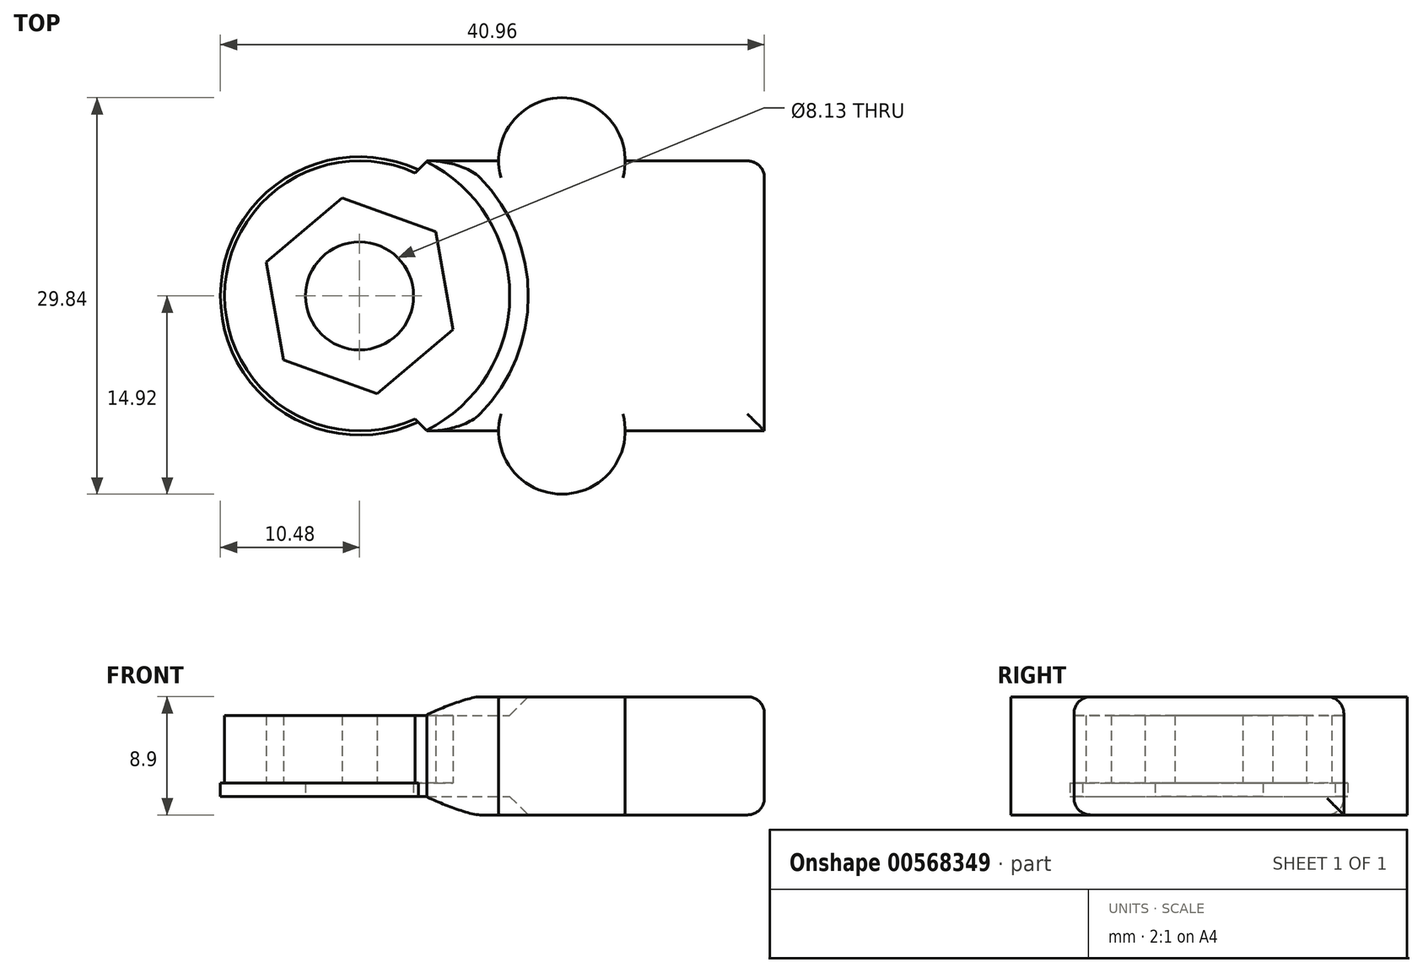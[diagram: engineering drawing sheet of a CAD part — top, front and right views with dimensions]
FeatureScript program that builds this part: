
annotation { "Feature Type Name" : "Feature", "Feature Type Description" : "" }
export const myFeature = defineFeature(function(context is Context, id is Id, definition is map)
    precondition{}
    {
        {
            var Q0;
            Q0=qCreatedBy(makeId("Top.planeOp"),FACE);
            var sketch = newSketch(context, id + "F0", { "sketchPlane" : qUnion([Q0])});
            skCircle(sketch, "E0.cCircle", {"center": v(0, 0) * mm, "radius": 6.48 * mm, "construction": true});
            skLineSegment(sketch, "E0.0", {"start": v(-7.03, 2.55) * mm, "end": v(-1.31, 7.36) * mm});
            skLineSegment(sketch, "E0.1", {"start": v(-1.31, 7.36) * mm, "end": v(5.72, 4.82) * mm});
            skLineSegment(sketch, "E0.2", {"start": v(5.72, 4.82) * mm, "end": v(7.03, -2.55) * mm});
            skLineSegment(sketch, "E0.3", {"start": v(7.03, -2.55) * mm, "end": v(1.31, -7.36) * mm});
            skLineSegment(sketch, "E0.4", {"start": v(1.31, -7.36) * mm, "end": v(-5.72, -4.82) * mm});
            skLineSegment(sketch, "E0.5", {"start": v(-5.72, -4.82) * mm, "end": v(-7.03, 2.55) * mm});
            skPoint(sketch, "E0.0.midPoint", {"position": v(-4.17, 4.95) * mm});
            skLineSegment(sketch, "E1.trimOffspring", {"start": v(4.6, -4.6) * mm, "end": v(4.58, -4.58) * mm});
            skCircle(sketch, "E2", {"center": v(0, 0) * mm, "radius": 10.16 * mm});
            skLineSegment(sketch, "E3.left", {"start": v(0, 10.2) * mm, "end": v(0, -10.12) * mm});
            skLineSegment(sketch, "E4.bottom", {"start": v(5.08, 10.16) * mm, "end": v(10.48, 10.16) * mm});
            skLineSegment(sketch, "E4.top", {"start": v(5.08, -10.16) * mm, "end": v(10.48, -10.16) * mm});
            skLineSegment(sketch, "E4.right", {"start": v(30.48, 10.16) * mm, "end": v(30.48, -10.16) * mm});
            skArc(sketch, "E5", {"start": v(20, 10.16) * mm, "mid": v(15.24, 14.92) * mm, "end": v(10.48, 10.16) * mm});
            skArc(sketch, "E6", {"start": v(10.48, -10.16) * mm, "mid": v(15.24, -14.92) * mm, "end": v(20, -10.16) * mm});
            skLineSegment(sketch, "E7", {"start": v(5.08, 10.16) * mm, "end": v(4.18, 9.26) * mm});
            skLineSegment(sketch, "E8", {"start": v(5.08, -10.16) * mm, "end": v(4.18, -9.26) * mm});
            skLineSegment(sketch, "E9.trimOffspring", {"start": v(20, 10.16) * mm, "end": v(30.48, 10.16) * mm});
            skLineSegment(sketch, "E10.trimOffspring", {"start": v(20, -10.16) * mm, "end": v(30.48, -10.16) * mm});
            skArc(sketch, "E11.MirrorCS", {"start": v(-20, 10.16) * mm, "mid": v(-15.24, 14.92) * mm, "end": v(-10.48, 10.16) * mm});
            skLineSegment(sketch, "E12.MirrorCS", {"start": v(-5.08, 10.16) * mm, "end": v(-10.48, 10.16) * mm});
            skLineSegment(sketch, "E13.MirrorCS", {"start": v(-5.08, 10.16) * mm, "end": v(-4.18, 9.26) * mm});
            skLineSegment(sketch, "E14.MirrorCS", {"start": v(-20, 10.16) * mm, "end": v(-30.48, 10.16) * mm});
            skLineSegment(sketch, "E15.MirrorCS", {"start": v(-30.48, 10.16) * mm, "end": v(-30.48, -10.16) * mm});
            skLineSegment(sketch, "E16.MirrorCS", {"start": v(-5.08, -10.16) * mm, "end": v(-4.18, -9.26) * mm});
            skArc(sketch, "E17.MirrorCS", {"start": v(-10.48, -10.16) * mm, "mid": v(-15.24, -14.92) * mm, "end": v(-20, -10.16) * mm});
            skLineSegment(sketch, "E18.MirrorCS", {"start": v(-5.08, -10.16) * mm, "end": v(-10.48, -10.16) * mm});
            skLineSegment(sketch, "E19.MirrorCS", {"start": v(-20, -10.16) * mm, "end": v(-30.48, -10.16) * mm});
            skSolve(sketch);
        }
        {
            var Q0;
            {var subQ4=sQuery(id+"F0.wireOp",EDGE,"E0.0");Q0=makeQuery(id+"F0.imprint","IMPRINT",FACE,{"disambiguationData":[TD([[makeQuery(id+"F0.imprint","IMPRINT",EDGE,{"derivedFrom":subQ4}),1.0]])]});}
            extrude(context, id + "F1", {"entities" : qUnion([Q0]), "endBound" : BoundingType.SYMMETRIC, "depth" : 6.1 * mm, "offsetDistance" : 25.4 * mm});
        }
        {
            var Q0;
            Q0=makeQuery(id+"F0.imprint","IMPRINT",FACE,{"disambiguationData":[TD([[makeQuery(id+"F0.imprint","IMPRINT",EDGE,{"derivedFrom":sQuery(id+"F0.wireOp",EDGE,"E11.MirrorCS")}),-1.0]])]});
            var Q1;
            Q1=makeQuery(id+"F0.imprint","IMPRINT",FACE,{"disambiguationData":[TD([[makeQuery(id+"F0.imprint","IMPRINT",EDGE,{"derivedFrom":sQuery(id+"F0.wireOp",EDGE,"E4.bottom")}),-1.0]])]});
            extrude(context, id + "F2", {"entities" : qUnion([Q0, Q1]), "operationType" : NewBodyOperationType.ADD, "endBound" : BoundingType.SYMMETRIC, "depth" : 8.9 * mm, "offsetDistance" : 25.4 * mm});
        }
        {
            var Q0;
            {var subQ0=sQuery(id+"F0.wireOp",EDGE,"E2");Q0=makeQuery(id+"F2.opExtrude","CAP_EDGE",EDGE,{"disambiguationData":[OSD([subQ0]),TDD([makeQuery(id+"F0.imprint","IMPRINT",EDGE,{"disambiguationData":[TD([[makeQuery(id+"F0.imprint","INTERSECT",VERTEX,{"derivedFrom":[subQ0,sQuery(id+"F0.wireOp",EDGE,"E13.MirrorCS")]}),-1.0]])],"derivedFrom":subQ0})])],"isStart":false});}
            var Q1;
            {var subQ0=sQuery(id+"F0.wireOp",EDGE,"E2");Q1=makeQuery(id+"F2.opExtrude","CAP_EDGE",EDGE,{"disambiguationData":[OSD([subQ0]),TDD([makeQuery(id+"F0.imprint","IMPRINT",EDGE,{"disambiguationData":[TD([[makeQuery(id+"F0.imprint","INTERSECT",VERTEX,{"derivedFrom":[subQ0,sQuery(id+"F0.wireOp",EDGE,"E7")]}),1.0]])],"derivedFrom":subQ0})])],"isStart":false});}
            var Q2;
            {var subQ0=sQuery(id+"F0.wireOp",EDGE,"E2");Q2=makeQuery(id+"F2.opExtrude","CAP_EDGE",EDGE,{"disambiguationData":[OSD([subQ0]),TDD([makeQuery(id+"F0.imprint","IMPRINT",EDGE,{"disambiguationData":[TD([[makeQuery(id+"F0.imprint","INTERSECT",VERTEX,{"derivedFrom":[subQ0,sQuery(id+"F0.wireOp",EDGE,"E7")]}),1.0]])],"derivedFrom":subQ0})])],"isStart":true});}
            var Q3;
            {var subQ0=sQuery(id+"F0.wireOp",EDGE,"E2");Q3=makeQuery(id+"F2.opExtrude","CAP_EDGE",EDGE,{"disambiguationData":[OSD([subQ0]),TDD([makeQuery(id+"F0.imprint","IMPRINT",EDGE,{"disambiguationData":[TD([[makeQuery(id+"F0.imprint","INTERSECT",VERTEX,{"derivedFrom":[subQ0,sQuery(id+"F0.wireOp",EDGE,"E13.MirrorCS")]}),-1.0]])],"derivedFrom":subQ0})])],"isStart":true});}
            chamfer(context, id + "F3", {"entities" : qUnion([Q0, Q1, Q2, Q3]), "width" : 2.54 * mm, "tangentPropagation" : true});
        }
        {
            var Q0;
            Q0=makeQuery(id+"F2.opExtrude","CAP_EDGE",EDGE,{"disambiguationData":[OSD([sQuery(id+"F0.wireOp",EDGE,"E19.MirrorCS")])],"isStart":false});
            var Q1;
            Q1=makeQuery(id+"F2.opExtrude","CAP_EDGE",EDGE,{"disambiguationData":[OSD([sQuery(id+"F0.wireOp",EDGE,"E15.MirrorCS")])],"isStart":false});
            var Q2;
            Q2=makeQuery(id+"F2.opExtrude","CAP_EDGE",EDGE,{"disambiguationData":[OSD([sQuery(id+"F0.wireOp",EDGE,"E14.MirrorCS")])],"isStart":false});
            var Q3;
            Q3=makeQuery(id+"F2.opExtrude","CAP_EDGE",EDGE,{"disambiguationData":[OSD([sQuery(id+"F0.wireOp",EDGE,"E10.trimOffspring")])],"isStart":false});
            var Q4;
            Q4=makeQuery(id+"F2.opExtrude","CAP_EDGE",EDGE,{"disambiguationData":[OSD([sQuery(id+"F0.wireOp",EDGE,"E4.right")])],"isStart":false});
            var Q5;
            Q5=makeQuery(id+"F2.opExtrude","CAP_EDGE",EDGE,{"disambiguationData":[OSD([sQuery(id+"F0.wireOp",EDGE,"E9.trimOffspring")])],"isStart":false});
            var Q6;
            Q6=makeQuery(id+"F2.opExtrude","CAP_EDGE",EDGE,{"disambiguationData":[OSD([sQuery(id+"F0.wireOp",EDGE,"E19.MirrorCS")])],"isStart":true});
            var Q7;
            Q7=makeQuery(id+"F2.opExtrude","SWEPT_EDGE",EDGE,{"disambiguationData":[OSD([sQuery(id+"F0.wireOp",EDGE,"E15.MirrorCS"),sQuery(id+"F0.wireOp",EDGE,"E19.MirrorCS")])]});
            var Q8;
            Q8=makeQuery(id+"F2.opExtrude","CAP_EDGE",EDGE,{"disambiguationData":[OSD([sQuery(id+"F0.wireOp",EDGE,"E10.trimOffspring")])],"isStart":true});
            var Q9;
            Q9=makeQuery(id+"F2.opExtrude","CAP_EDGE",EDGE,{"disambiguationData":[OSD([sQuery(id+"F0.wireOp",EDGE,"E4.right")])],"isStart":true});
            var Q10;
            Q10=makeQuery(id+"F2.opExtrude","SWEPT_EDGE",EDGE,{"disambiguationData":[OSD([sQuery(id+"F0.wireOp",EDGE,"E4.right"),sQuery(id+"F0.wireOp",EDGE,"E9.trimOffspring")])]});
            var Q11;
            Q11=makeQuery(id+"F2.opExtrude","SWEPT_EDGE",EDGE,{"disambiguationData":[OSD([sQuery(id+"F0.wireOp",EDGE,"E14.MirrorCS"),sQuery(id+"F0.wireOp",EDGE,"E15.MirrorCS")])]});
            var Q12;
            Q12=makeQuery(id+"F2.opExtrude","CAP_EDGE",EDGE,{"disambiguationData":[OSD([sQuery(id+"F0.wireOp",EDGE,"E14.MirrorCS")])],"isStart":true});
            var Q13;
            Q13=makeQuery(id+"F2.opExtrude","CAP_EDGE",EDGE,{"disambiguationData":[OSD([sQuery(id+"F0.wireOp",EDGE,"E15.MirrorCS")])],"isStart":true});
            var Q14;
            Q14=makeQuery(id+"F2.opExtrude","CAP_EDGE",EDGE,{"disambiguationData":[OSD([sQuery(id+"F0.wireOp",EDGE,"E12.MirrorCS")])],"isStart":false});
            var Q15;
            Q15=makeQuery(id+"F2.opExtrude","CAP_EDGE",EDGE,{"disambiguationData":[OSD([sQuery(id+"F0.wireOp",EDGE,"E4.bottom")])],"isStart":false});
            var Q16;
            Q16=makeQuery(id+"F2.opExtrude","CAP_EDGE",EDGE,{"disambiguationData":[OSD([sQuery(id+"F0.wireOp",EDGE,"E18.MirrorCS")])],"isStart":false});
            var Q17;
            Q17=makeQuery(id+"F2.opExtrude","CAP_EDGE",EDGE,{"disambiguationData":[OSD([sQuery(id+"F0.wireOp",EDGE,"E4.top")])],"isStart":false});
            var Q18;
            Q18=makeQuery(id+"F2.opExtrude","CAP_EDGE",EDGE,{"disambiguationData":[OSD([sQuery(id+"F0.wireOp",EDGE,"E4.bottom")])],"isStart":true});
            var Q19;
            Q19=makeQuery(id+"F2.opExtrude","CAP_EDGE",EDGE,{"disambiguationData":[OSD([sQuery(id+"F0.wireOp",EDGE,"E12.MirrorCS")])],"isStart":true});
            var Q20;
            Q20=makeQuery(id+"F2.opExtrude","CAP_EDGE",EDGE,{"disambiguationData":[OSD([sQuery(id+"F0.wireOp",EDGE,"E18.MirrorCS")])],"isStart":true});
            var Q21;
            Q21=makeQuery(id+"F2.opExtrude","CAP_EDGE",EDGE,{"disambiguationData":[OSD([sQuery(id+"F0.wireOp",EDGE,"E4.top")])],"isStart":true});
            fillet(context, id + "F4", {"entities" : qUnion([Q0, Q1, Q2, Q3, Q4, Q5, Q6, Q7, Q8, Q9, Q10, Q11, Q12, Q13, Q14, Q15, Q16, Q17, Q18, Q19, Q20, Q21]), "radius" : 1.27 * mm, "tangentPropagation" : true, "allowEdgeOverflow" : false});
        }
        {
            var Q0;
            Q0=makeQuery(id+"F1.opExtrude","CAP_FACE",FACE,{"disambiguationData":[OSD([sQuery(id+"F0.wireOp",EDGE,"E0.0"),sQuery(id+"F0.wireOp",EDGE,"E0.1"),sQuery(id+"F0.wireOp",EDGE,"E0.2"),sQuery(id+"F0.wireOp",EDGE,"E0.3"),sQuery(id+"F0.wireOp",EDGE,"E0.4"),sQuery(id+"F0.wireOp",EDGE,"E0.5"),sQuery(id+"F0.wireOp",EDGE,"RWQ8MwqZ-qSjk-59TD-cotx-tmdDIhJuCybJ")])],"isStart":true});
            var sketch = newSketch(context, id + "F5", { "sketchPlane" : qUnion([Q0])});
            skCircle(sketch, "E20", {"center": v(0, 0) * mm, "radius": 10.48 * mm});
            skCircle(sketch, "E21", {"center": v(0, 0) * mm, "radius": 4.06 * mm});
            skSolve(sketch);
        }
        {
            var Q0;
            Q0=makeQuery(id+"F5.imprint","IMPRINT",FACE,{"disambiguationData":[TD([[makeQuery(id+"F5.imprint","IMPRINT",EDGE,{"derivedFrom":sQuery(id+"F5.wireOp",EDGE,"E20")}),1.0]])]});
            var Q1;
            Q1=makeQuery(id+"F5.imprint","IMPRINT",FACE,{"disambiguationData":[TD([[makeQuery(id+"F5.imprint","IMPRINT",EDGE,{"derivedFrom":sQuery(id+"F5.wireOp",EDGE,"E21")}),-1.0]])]});
            extrude(context, id + "F6", {"entities" : qUnion([Q0, Q1]), "operationType" : NewBodyOperationType.ADD, "oppositeDirection" : true, "depth" : 1.02 * mm, "offsetDistance" : 25.4 * mm});
        }
    });
